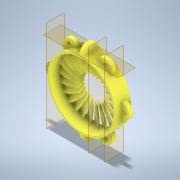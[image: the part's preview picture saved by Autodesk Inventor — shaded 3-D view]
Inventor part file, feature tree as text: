
AUTODESK INVENTOR PART (.ipt)
format: ipt  version: 2021.2 (Build 252289000, 289)  size: 910,336 bytes
history: native  units: in
note: dims shown in document units (in); Inventor stores cm internally (conversion verified against a paired STEP export)
features: sketch x9, extrude x8, plane x4, pattern_circular x3, fillet x2, loft x1, other x1
ambient origin geometry x8: Origin, YZ Plane, XZ Plane, XY Plane, X Axis, Y Axis, Z Axis, Center Point
bodies: Solid1 (feature_tree)
feature tree (28):
  extrude  "Extrusion1"  Depth=4.25in
  plane  "Work Plane2"
  extrude  "Extrusion3"  Depth=2.125in
  fillet  "Fillet1"  Radius=0.25in
  extrude  "Extrusion4"  Depth=0.5in TaperAngle=0.0deg
  pattern_circular  "Circular Pattern2"  Count=2 Angle=360.0deg
  plane  "Work Plane3"
  extrude  "Extrusion5"  Depth=1.0in
  extrude  "Extrusion6"  Depth=0.5in
  fillet  "Fillet2"  [1 undecoded]
  extrude  "Extrusion7"  Depth=0.1in TaperAngle=0.0deg
  pattern_circular  "Circular Pattern3"  [2 undecoded]
  plane  "Work Plane4"
  plane  "Work Plane6"
  sketch  "Sketch13"  dims[d18=0.5in d19=0.0in d20=0.7874in d21=360.0deg]
  extrude  "Extrusion15"  Depth=0.5in
  loft  "Loft5"
  pattern_circular  "Circular Pattern9"  [2 undecoded]
  extrude  "Extrusion16"  Depth=0.5in TaperAngle=0.0deg
  sketch  "Sketch1"  dims[d0=4.0in d1=4.25in]
  sketch  "Sketch3"  dims[d2=1.0in d3=0.0in d10=2.125in d11=0.25in]
  sketch  "Sketch4"  dims[d12=0.0in d13=0.5in d14=0.0in]
  sketch  "Sketch5"  dims[d15=0.5in]
  sketch  "Sketch6"  dims[d16=0.125in]
  sketch  "Sketch7"  dims[d17=0.2in]
  sketch  "Sketch16"  dims[d23=-2.125in d24=1.0in]
  other  "Edges5"
  sketch  "Sketch18"  dims[d25=0.25in d26=0.5in d27=0.0in d28=0.1in d29=0.0in d30=0.5in d31=0.0in d32=0.5in d33=0.25in d34=0.2in d35=0.5in d36=0.0in d37=2.3622in d38=360.0deg d40=0.25in d41=0.125in d42=0.25in d43=0.2in d49=0.5in d75=1.5in d111=0.5in d112=0.0312in d113=0.5in d114=0.0in d115=0.0in d116=90.0deg d117=0.0in d118=90.0deg d119=9.4488in d120=360.0deg d122=1.4625in d123=0.0in d124=0.0777in d79=0.5in d80=0.0344in d81=0.5in d82=0.0344in]
note: 5 required parameter values undecoded (feature->parameter linkage not recoverable at this tier; creation-order binding heuristic only, values carry confidence <= 0.55)
